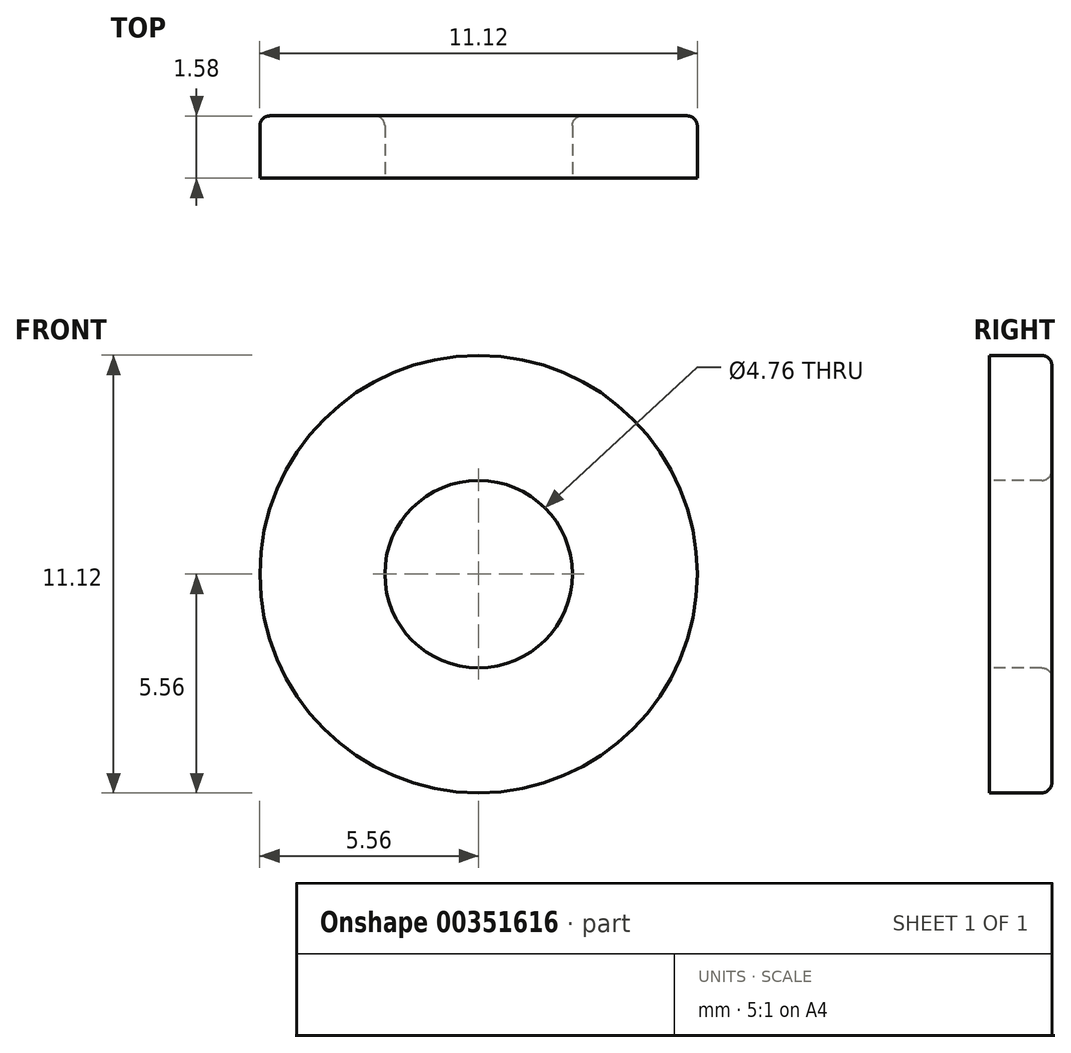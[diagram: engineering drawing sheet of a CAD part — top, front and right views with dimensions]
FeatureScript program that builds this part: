
annotation { "Feature Type Name" : "Feature", "Feature Type Description" : "" }
export const myFeature = defineFeature(function(context is Context, id is Id, definition is map)
    precondition{}
    {
        {
            var Q0;
            Q0=qCreatedBy(makeId("Front.planeOp"),FACE);
            var sketch = newSketch(context, id + "F0", { "sketchPlane" : qUnion([Q0])});
            skCircle(sketch, "E0", {"center": v(0, 0) * mm, "radius": 5.56 * mm});
            skSolve(sketch);
        }
        {
            var Q0;
            Q0 = qSketchRegion(id + "F0", true);
            extrude(context, id + "F1", {"entities" : qUnion([Q0]), "depth" : 1.59 * mm, "symmetric" : true});
        }
        {
            var Q0;
            Q0=qCreatedBy(makeId("Front.planeOp"),FACE);
            var sketch = newSketch(context, id + "F2", { "sketchPlane" : qUnion([Q0])});
            skCircle(sketch, "E1", {"center": v(0, 0) * mm, "radius": 2.38 * mm});
            skSolve(sketch);
        }
        {
            var Q0;
            Q0 = qSketchRegion(id + "F2", true);
            extrude(context, id + "F3", {"entities" : qUnion([Q0]), "operationType" : NewBodyOperationType.REMOVE, "oppositeDirection" : true, "depth" : 50.8 * mm, "symmetric" : true});
        }
        {
            var Q0;
            Q0=makeQuery(id+"F3.boolean.opBoolean","INTERSECT",EDGE,{"derivedFrom":[makeQuery(id+"F1.opExtrude","CAP_FACE",FACE,{"disambiguationData":[OSD([sQuery(id+"F0.wireOp",EDGE,"E0")])],"isStart":true}),makeQuery(id+"F3.opExtrude","SWEPT_FACE",FACE,{"disambiguationData":[OSD([sQuery(id+"F2.wireOp",EDGE,"E1")])]})]});
            fillet(context, id + "F4", {"entities" : qUnion([Q0]), "radius" : 0.25 * mm, "tangentPropagation" : true, "allowEdgeOverflow" : false});
        }
        {
            var Q0;
            Q0=makeQuery(id+"F1.opExtrude","CAP_EDGE",EDGE,{"disambiguationData":[OSD([sQuery(id+"F0.wireOp",EDGE,"E0")])],"isStart":true});
            fillet(context, id + "F5", {"entities" : qUnion([Q0]), "radius" : 0.25 * mm, "tangentPropagation" : true, "allowEdgeOverflow" : false});
        }
    });
